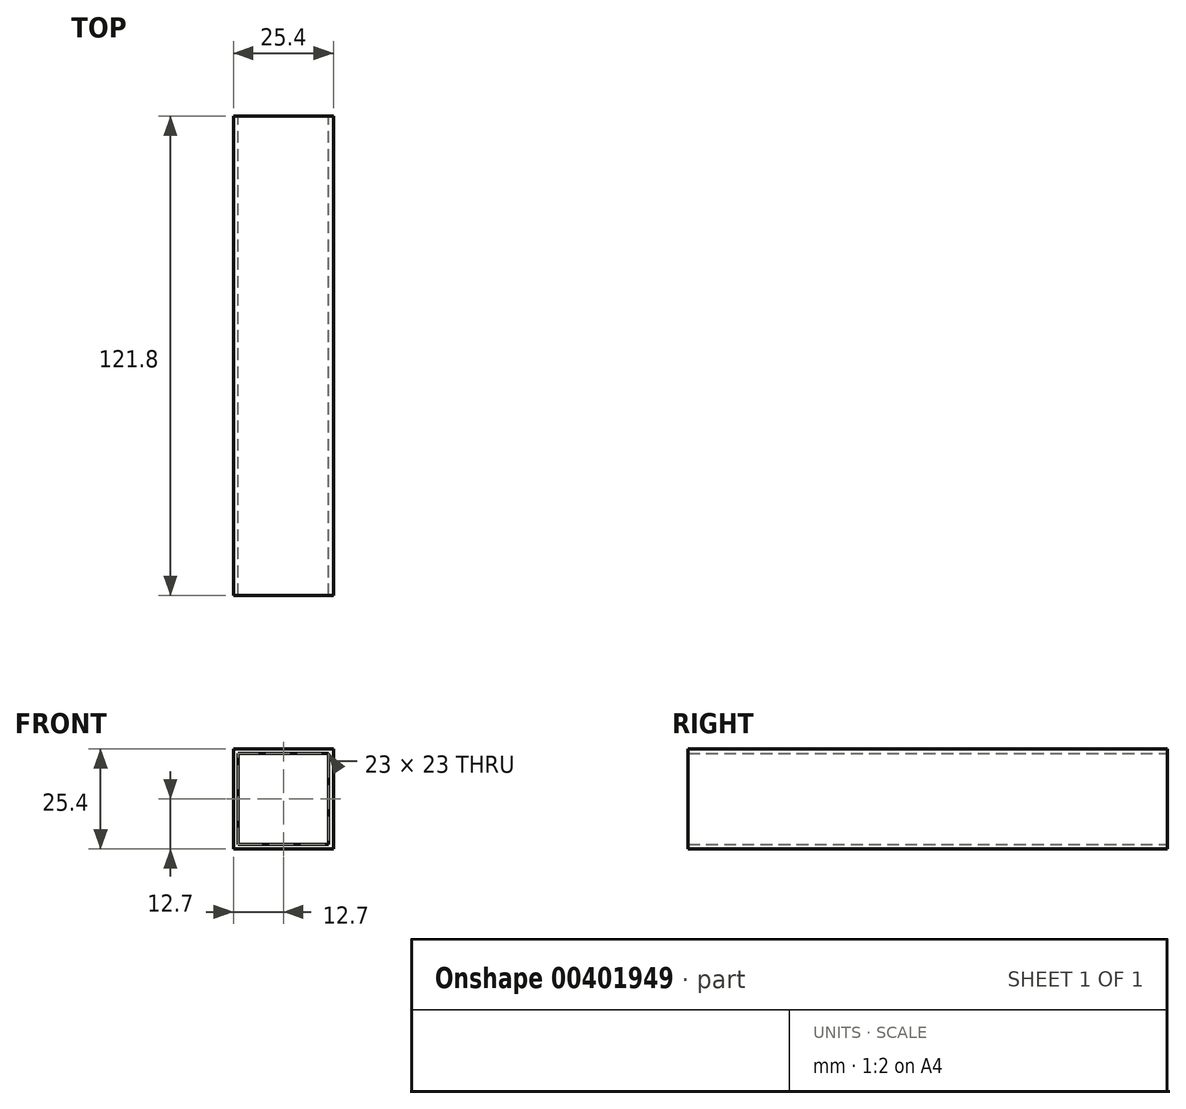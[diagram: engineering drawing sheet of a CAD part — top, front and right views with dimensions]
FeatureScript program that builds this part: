
annotation { "Feature Type Name" : "Feature", "Feature Type Description" : "" }
export const myFeature = defineFeature(function(context is Context, id is Id, definition is map)
    precondition{}
    {
        {
            var Q0;
            Q0=qCreatedBy(makeId("Front.planeOp"),FACE);
            var sketch = newSketch(context, id + "F0", { "sketchPlane" : qUnion([Q0])});
            skLineSegment(sketch, "E0.bottom", {"start": v(-12.7, 12.7) * mm, "end": v(12.7, 12.7) * mm});
            skLineSegment(sketch, "E0.top", {"start": v(-12.7, -12.7) * mm, "end": v(12.7, -12.7) * mm});
            skLineSegment(sketch, "E0.left", {"start": v(-12.7, 12.7) * mm, "end": v(-12.7, -12.7) * mm});
            skLineSegment(sketch, "E0.right", {"start": v(12.7, 12.7) * mm, "end": v(12.7, -12.7) * mm});
            skLineSegment(sketch, "E1", {"start": v(0, 0) * mm, "end": v(0, 12.7) * mm, "construction": true});
            skLineSegment(sketch, "E2", {"start": v(0, 0) * mm, "end": v(-12.7, 0) * mm, "construction": true});
            skLineSegment(sketch, "E3.0", {"start": v(-11.5, -11.5) * mm, "end": v(11.5, -11.5) * mm});
            skLineSegment(sketch, "E3.1", {"start": v(-11.5, 11.5) * mm, "end": v(-11.5, -11.5) * mm});
            skLineSegment(sketch, "E3.2", {"start": v(-11.5, 11.5) * mm, "end": v(11.5, 11.5) * mm});
            skLineSegment(sketch, "E3.3", {"start": v(11.5, 11.5) * mm, "end": v(11.5, -11.5) * mm});
            skSolve(sketch);
        }
        {
            var Q0;
            Q0=qSketchRegion(id+"F0",true);
            var Q1;
            Q1=qConstructionFilter(qBodyType(qCreatedBy(id+"F0",EDGE),BodyType.WIRE),ConstructionObject.NO);
            extrude(context, id + "F1", {"entities" : qUnion([Q0]), "surfaceEntities" : qUnion([Q1]), "endBound" : BoundingType.SYMMETRIC, "depth" : (115.8 + 6) * mm});
        }
        {
            var Q0;
            Q0=qCreatedBy(makeId("Top.planeOp"),FACE);
            var sketch = newSketch(context, id + "F2", { "sketchPlane" : qUnion([Q0])});
            skLineSegment(sketch, "E4.0.0", {"start": v(12.7, 60.9) * mm, "end": v(-12.7, 60.9) * mm});
            skLineSegment(sketch, "E4.0.1", {"start": v(-12.7, 60.9) * mm, "end": v(-12.7, -60.9) * mm});
            skLineSegment(sketch, "E4.0.2", {"start": v(-12.7, -60.9) * mm, "end": v(12.7, -60.9) * mm});
            skLineSegment(sketch, "E4.0.3", {"start": v(12.7, -60.9) * mm, "end": v(12.7, 60.9) * mm});
            skSolve(sketch);
        }
    });
